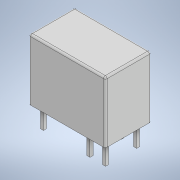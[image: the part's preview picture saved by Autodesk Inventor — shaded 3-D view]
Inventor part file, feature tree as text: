
AUTODESK INVENTOR PART (.ipt)
format: ipt  version: 2021.2 (Build 252289000, 289)  size: 145,408 bytes
history: native  units: mm
features: extrude x2, sketch x2, other x1, fillet x1
ambient origin geometry x8: Origin, YZ Plane, XZ Plane, XY Plane, X Axis, Y Axis, Z Axis, Center Point
bodies: Body1 (feature_tree)
feature tree (6):
  other  "Твердое тело1"
  extrude  "Выдавливание1"  Depth=12.5mm
  extrude  "Выдавливание2"  Depth=7.5mm
  fillet  "Сопряжение1"  Radius=10.0mm
  sketch  "Эскиз1"
  sketch  "Эскиз2"
